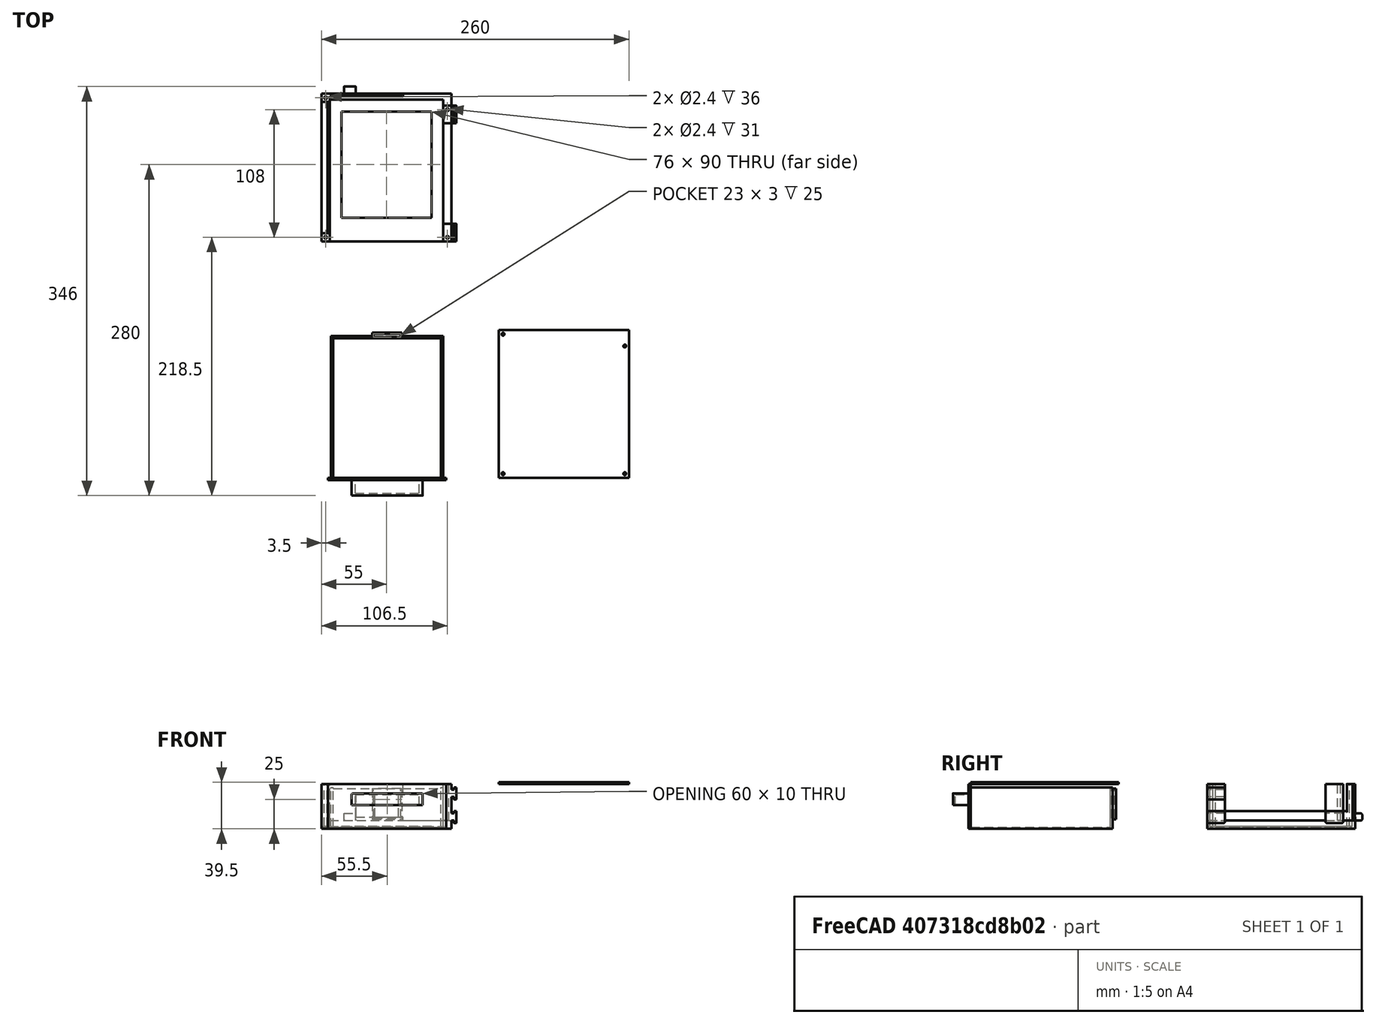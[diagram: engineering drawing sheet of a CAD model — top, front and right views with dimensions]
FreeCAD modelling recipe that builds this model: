
FCSTD DOCUMENT  (FreeCAD 0.19R)
Label: FiokaZaAlat
License: All rights reserved
LicenseURL: http://en.wikipedia.org/wiki/All_rights_reserved
objects: Part::Box×29, Part::Fillet×10, Part::Cut×9, Part::Cylinder×8, Part::MultiFuse×7
note: 63 computed .brp shape members not serialized (recipe doc carries the construction recipe); baked Part::Feature solids carry a one-line shape summary decoded from their .brp

FEATURE [Part::Box] Box001  label="TeloKlizaca1"
  AttacherType = Attacher::AttachEngine3D
  Height = 6
  Length = 6
  Placement = pos=(15,-40,7) rot=(0,0,1;0rad)
  Width = 15
FEATURE [Part::Box] Box002  label="ZubKlizaca1"
  AttacherType = Attacher::AttachEngine3D
  Height = 10
  Length = 2
  Placement = pos=(19,-40,5) rot=(0,0,1;0rad)
  Width = 15
FEATURE [Part::Box] Box010  label="PovrsinaDna"
  AttacherType = Attacher::AttachEngine3D
  Height = 2
  Length = 110
  Placement = pos=(-94,-50,0) rot=(0,0,1;0rad)
  Width = 125
FEATURE [Part::Box] Box012  label="RupaDna"
  AttacherType = Attacher::AttachEngine3D
  Height = 5
  Length = 76
  Placement = pos=(-77,-30,0) rot=(0,0,1;0rad)
  Width = 90
FEATURE [Part::Box] Box013  label="PovrsinaZadnjeStrane"
  AttacherType = Attacher::AttachEngine3D
  Height = 38
  Length = 62
  Placement = pos=(-87,73,0) rot=(0,0,1;0rad)
  Width = 2
FEATURE [Part::Box] Box015  label="RupaLedja002"
  AttacherType = Attacher::AttachEngine3D
  Height = 20
  Length = 70
  Placement = pos=(-65,73,10) rot=(0,0,1;0rad)
  Width = 10
FEATURE [Part::Box] Box016  label="StranaLeva"
  AttacherType = Attacher::AttachEngine3D
  Height = 15
  Length = 2
  Placement = pos=(-89,-48,0) rot=(0,0,1;0rad)
  Width = 123
FEATURE [Part::Box] Box018  label="PovrsinaPlafona"
  AttacherType = Attacher::AttachEngine3D
  Height = 1.5
  Length = 110
  Placement = pos=(-94,-50,38) rot=(0,0,1;0rad)
  Width = 125
FEATURE [Part::Box] Box020  label="DnoFioke"
  AttacherType = Attacher::AttachEngine3D
  Height = 1.5
  Length = 95
  Placement = pos=(-86,-50,0) rot=(0,0,1;0rad)
  Width = 120
FEATURE [Part::Box] Box021  label="StranaFiokeDesna"
  AttacherType = Attacher::AttachEngine3D
  Height = 35
  Length = 2
  Placement = pos=(7,-50,0) rot=(0,0,1;0rad)
  Width = 120
FEATURE [Part::Box] Box022  label="StranaFiokeLeva"
  AttacherType = Attacher::AttachEngine3D
  Height = 35
  Length = 2
  Placement = pos=(-86,-50,0) rot=(0,0,1;0rad)
  Width = 120
FEATURE [Part::Box] Box023  label="TeloledjaFioke"
  AttacherType = Attacher::AttachEngine3D
  Height = 34
  Length = 95
  Placement = pos=(-86,68,0) rot=(0,0,1;0rad)
  Width = 2
FEATURE [Part::Box] Box024  label="FrontFioke"
  AttacherType = Attacher::AttachEngine3D
  Height = 38
  Length = 100
  Placement = pos=(-88.5,-52,0) rot=(0,0,1;0rad)
  Width = 2
FEATURE [Part::Box] Box025  label="TeloRucke"
  AttacherType = Attacher::AttachEngine3D
  Height = 10
  Length = 60
  Placement = pos=(-58.5,-65,20) rot=(0,0,1;0rad)
  Width = 15
FEATURE [Part::Box] Box026  label="RupaRucke"
  AttacherType = Attacher::AttachEngine3D
  Height = 9
  Length = 54
  Placement = pos=(-55.5,-63,20) rot=(0,0,1;0rad)
  Width = 11
FEATURE [Part::Cut] Cut008
  Base = -> Box025
  Tool = -> Box026
FEATURE [Part::Fillet] Fillet002
  Base = -> Cut008
  Edges = 1 edges r=1: [Edge2]
FEATURE [Part::Fillet] Fillet003  label="Rucka"
  Base = -> Fillet002
  Edges = 1 edges r=1: [Edge19]
  Placement = pos=(-10,0,0) rot=(0,0,1;0rad)
FEATURE [Part::Box] Box027  label="KutijaMagneta"
  AttacherType = Attacher::AttachEngine3D
  Height = 26
  Length = 25
  Placement = pos=(-51,68,8) rot=(0,0,1;0rad)
  Width = 5
FEATURE [Part::Box] Box028  label="RupaMagneta"
  AttacherType = Attacher::AttachEngine3D
  Height = 26
  Length = 23
  Placement = pos=(-50,69,9) rot=(0,0,1;0rad)
  Width = 3
FEATURE [Part::Box] Box029  label="Slabljenje"
  AttacherType = Attacher::AttachEngine3D
  Height = 20
  Length = 20
  Placement = pos=(-49,73,10) rot=(0,0,1;0rad)
  Width = 1.8
FEATURE [Part::MultiFuse] Fusion012
  Shapes = -> [Fillet003,Box020,Box021,Box022,Box023,Box024,Box027]
FEATURE [Part::Cut] Cut009  label="Fioka"
  Base = -> Fusion012
  Tool = -> Box028
FEATURE [Part::Fillet] Fillet
  Base = -> Box002
  Edges = 4 edges r=1: [Edge9,Edge10,Edge11,Edge12]
FEATURE [Part::MultiFuse] Fusion  label="Klizac001"
  Placement = pos=(0,-10,0) rot=(0,0,1;0rad)
  Shapes = -> [Box001,Fillet]
FEATURE [Part::Box] Box030  label="ZubKlizaca002"
  AttacherType = Attacher::AttachEngine3D
  Height = 10
  Length = 2
  Placement = pos=(19,-40,5) rot=(0,0,1;0rad)
  Width = 15
FEATURE [Part::Box] Box031  label="TeloKlizaca002"
  AttacherType = Attacher::AttachEngine3D
  Height = 6
  Length = 6
  Placement = pos=(15,-40,7) rot=(0,0,1;0rad)
  Width = 15
FEATURE [Part::Fillet] Fillet004
  Base = -> Box030
  Edges = 4 edges r=1: [Edge9,Edge10,Edge11,Edge12]
FEATURE [Part::MultiFuse] Fusion016  label="Klizac002"
  Placement = pos=(0,90,0) rot=(0,0,1;0rad)
  Shapes = -> [Box031,Fillet004]
FEATURE [Part::Box] Box032  label="TeloKlizaca003"
  AttacherType = Attacher::AttachEngine3D
  Height = 6
  Length = 6
  Placement = pos=(15,-40,7) rot=(0,0,1;0rad)
  Width = 15
FEATURE [Part::Box] Box033  label="ZubKlizaca003"
  AttacherType = Attacher::AttachEngine3D
  Height = 10
  Length = 2
  Placement = pos=(19,-40,5) rot=(0,0,1;0rad)
  Width = 15
FEATURE [Part::Fillet] Fillet005
  Base = -> Box033
  Edges = 4 edges r=1: [Edge9,Edge10,Edge11,Edge12]
FEATURE [Part::MultiFuse] Fusion017  label="Klizac003"
  Placement = pos=(0,-10,20) rot=(0,0,1;0rad)
  Shapes = -> [Box032,Fillet005]
FEATURE [Part::Box] Box035  label="zub4"
  AttacherType = Attacher::AttachEngine3D
  Height = 6
  Length = 10
  Placement = pos=(-75,75,7) rot=(0,0,1;0rad)
  Width = 6
FEATURE [Part::Cut] Cut  label="ZadnjaStrana"
  Base = -> Box013
  Tool = -> Box015
FEATURE [Part::Box] Box036  label="Sraf001"
  AttacherType = Attacher::AttachEngine3D
  Height = 38
  Length = 7
  Placement = pos=(-94,68,0) rot=(0,0,1;0rad)
  Width = 7
FEATURE [Part::Box] Box037  label="Sraf002"
  AttacherType = Attacher::AttachEngine3D
  Height = 38
  Length = 7
  Placement = pos=(-94,-50,0) rot=(0,0,1;0rad)
  Width = 7
FEATURE [Part::Cylinder] Cylinder  label="Rupa001"
  Angle = 360
  AttacherType = Attacher::AttachEngine3D
  Height = 80
  Placement = pos=(-90.5,71.5,0) rot=(0,0,1;0rad)
  Radius = 1.2
FEATURE [Part::Cut] Cut012
  Base = -> Box036
  Tool = -> Cylinder
FEATURE [Part::Cylinder] Cylinder001  label="Rupa002"
  Angle = 360
  AttacherType = Attacher::AttachEngine3D
  Height = 80
  Placement = pos=(-90.5,-46.5,0) rot=(0,0,1;0rad)
  Radius = 1.2
FEATURE [Part::Cut] Cut013
  Base = -> Box037
  Tool = -> Cylinder001
FEATURE [Part::Box] Box040  label="OjacanjeStraneDesne"
  AttacherType = Attacher::AttachEngine3D
  Height = 7
  Length = 7
  Placement = pos=(9,-49,0) rot=(0,0,1;0rad)
  Width = 124
FEATURE [Part::Box] Box041  label="Sraf003"
  AttacherType = Attacher::AttachEngine3D
  Height = 38
  Length = 7
  Placement = pos=(-101,60,0) rot=(0,0,1;0rad)
  Width = 15
FEATURE [Part::Cylinder] Cylinder006  label="Rupa007"
  Angle = 360
  AttacherType = Attacher::AttachEngine3D
  Height = 80
  Placement = pos=(-97.5,71.5,0) rot=(0,0,1;0rad)
  Radius = 1.2
FEATURE [Part::Cut] Cut016
  Base = -> Box041
  Placement = pos=(110,-10,0) rot=(0,0,1;0rad)
  Tool = -> Cylinder006
FEATURE [Part::Box] Box042  label="Sraf004"
  AttacherType = Attacher::AttachEngine3D
  Height = 38
  Length = 7
  Placement = pos=(-100,-50,0) rot=(0,0,1;0rad)
  Width = 15
FEATURE [Part::Cylinder] Cylinder007  label="Rupa008"
  Angle = 360
  AttacherType = Attacher::AttachEngine3D
  Height = 80
  Placement = pos=(-96.5,-46.5,0) rot=(0,0,1;0rad)
  Radius = 1.2
FEATURE [Part::Cut] Cut017
  Base = -> Box042
  Placement = pos=(109,0,0) rot=(0,0,1;0rad)
  Tool = -> Cylinder007
FEATURE [Part::Cylinder] Cylinder008  label="Rupa009"
  Angle = 360
  AttacherType = Attacher::AttachEngine3D
  Height = 80
  Placement = pos=(-90.5,-46.5,0) rot=(0,0,1;0rad)
  Radius = 1.2
FEATURE [Part::Cylinder] Cylinder009  label="Rupa010"
  Angle = 360
  AttacherType = Attacher::AttachEngine3D
  Height = 80
  Placement = pos=(-90.5,71.5,0) rot=(0,0,1;0rad)
  Radius = 1.2
FEATURE [Part::Cylinder] Cylinder010  label="Rupa011"
  Angle = 360
  AttacherType = Attacher::AttachEngine3D
  Height = 80
  Placement = pos=(12.5,61.5,0) rot=(0,0,1;0rad)
  Radius = 1.2
FEATURE [Part::Cylinder] Cylinder011  label="Rupa012"
  Angle = 360
  AttacherType = Attacher::AttachEngine3D
  Height = 80
  Placement = pos=(12.5,-46.5,0) rot=(0,0,1;0rad)
  Radius = 1.2
FEATURE [Part::MultiFuse] Fusion021  label="RupePoklopca"
  Shapes = -> [Cylinder011,Cylinder009,Cylinder008,Cylinder010]
FEATURE [Part::Cut] Cut018  label="Poklopac"
  Base = -> Box018
  Placement = pos=(150,0,0) rot=(0,0,1;0rad)
  Tool = -> Fusion021
FEATURE [Part::Fillet] Fillet006  label="SrafZadnjiDesni"
  Base = -> Cut016
  Edges = 1 edges r=1: [Edge1]
FEATURE [Part::Fillet] Fillet008  label="SrafPrednjiDesni"
  Base = -> Cut017
  Edges = 1 edges r=1: [Edge1]
FEATURE [Part::Fillet] Fillet009  label="SrafPrednjiLevi"
  Base = -> Cut013
  Edges = 1 edges r=1: [Edge6]
FEATURE [Part::Fillet] Fillet010  label="SrafZadnjiLevi"
  Base = -> Cut012
  Edges = 1 edges r=1: [Edge6]
FEATURE [Part::Box] Box043  label="OjacanjeZadnjeStrane"
  AttacherType = Attacher::AttachEngine3D
  Height = 7
  Length = 96
  Placement = pos=(-87,70,0) rot=(0,0,1;0rad)
  Width = 5
FEATURE [Part::MultiFuse] Fusion022  label="Klizaci"
  Placement = pos=(-1,0,0) rot=(0,0,1;0rad)
  Shapes = -> [Fusion017,Fusion,Fusion016]
FEATURE [Part::Fillet] Fillet012  label="ZadnjiZub"
  Base = -> Box035
  Edges = 2 edges r=1: [Edge11,Edge12]
FEATURE [Part::Cut] Cut019  label="Dno"
  Base = -> Box010
  Tool = -> Box012
FEATURE [Part::MultiFuse] Fusion023  label="Kutija"
  Placement = pos=(0,200,0) rot=(0,0,1;0rad)
  Shapes = -> [Box016,Box029,Cut,Box040,Fillet006,Fillet008,Fillet009,Fillet010,Box043,Fusion022,Fillet012,Cut019]
